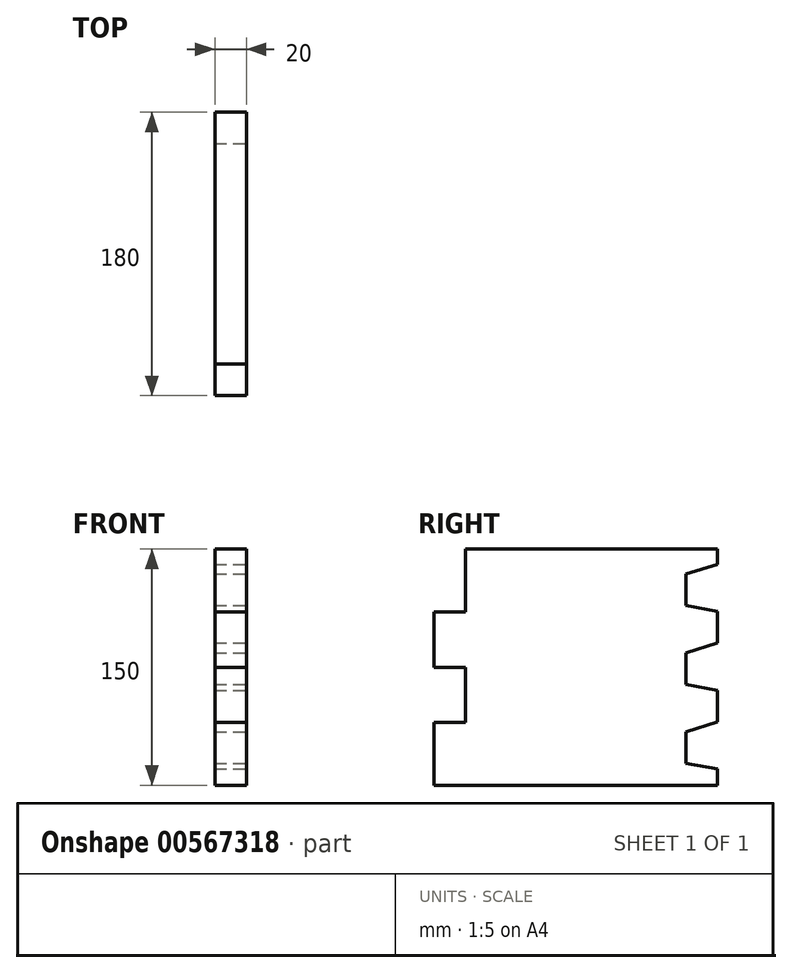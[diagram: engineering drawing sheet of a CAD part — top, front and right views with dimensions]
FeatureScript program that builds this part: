
annotation { "Feature Type Name" : "Feature", "Feature Type Description" : "" }
export const myFeature = defineFeature(function(context is Context, id is Id, definition is map)
    precondition{}
    {
        {
            var Q0;
            Q0=qCreatedBy(makeId("Front.planeOp"),FACE);
            var sketch = newSketch(context, id + "F0", { "sketchPlane" : qUnion([Q0])});
            skLineSegment(sketch, "E0.bottom", {"start": v(0, 0) * mm, "end": v(-180, 0) * mm});
            skLineSegment(sketch, "E0.top", {"start": v(0, 150) * mm, "end": v(-160, 150) * mm});
            skLineSegment(sketch, "E0.left", {"start": v(0, 0) * mm, "end": v(0, 150) * mm});
            skLineSegment(sketch, "E0.right", {"start": v(-180, 0) * mm, "end": v(-180, 40) * mm});
            skLineSegment(sketch, "E1", {"start": v(-160, 150) * mm, "end": v(-160, 0) * mm});
            skLineSegment(sketch, "E2", {"start": v(-180, 75) * mm, "end": v(-160, 75) * mm});
            skLineSegment(sketch, "E3", {"start": v(-160, 110) * mm, "end": v(-180, 110) * mm});
            skLineSegment(sketch, "E4", {"start": v(-160, 40) * mm, "end": v(-180, 40) * mm});
            skPoint(sketch, "E5.orphan", {"position": v(-180, 150) * mm});
            skLineSegment(sketch, "E6.trimOffspring", {"start": v(-180, 75) * mm, "end": v(-180, 110) * mm});
            skSolve(sketch);
        }
        {
            var Q0;
            Q0 = qSketchRegion(id + "F0", true);
            extrude(context, id + "F1", {"entities" : qUnion([Q0]), "depth" : 20 * mm, "offsetDistance" : 25 * mm});
        }
        {
            var Q0;
            Q0=makeQuery(id+"F1.opExtrude","SWEPT_FACE",FACE,{"disambiguationData":[OSD([sQuery(id+"F0.wireOp",EDGE,"E0.left")])]});
            var sketch = newSketch(context, id + "F2", { "sketchPlane" : qUnion([Q0])});
            skLineSegment(sketch, "E7", {"start": v(-20, 75) * mm, "end": v(0, 75) * mm});
            skLineSegment(sketch, "E8", {"start": v(-20, 60) * mm, "end": v(0, 65) * mm});
            skLineSegment(sketch, "E9", {"start": v(0, 85) * mm, "end": v(-20, 90) * mm});
            skLineSegment(sketch, "E10", {"start": v(-20, 90) * mm, "end": v(-20, 110) * mm});
            skLineSegment(sketch, "E11", {"start": v(0, 85) * mm, "end": v(0, 115) * mm});
            skLineSegment(sketch, "E12", {"start": v(0, 115) * mm, "end": v(-20, 110) * mm});
            skLineSegment(sketch, "E13", {"start": v(-20, 110) * mm, "end": v(-20, 140) * mm});
            skLineSegment(sketch, "E14", {"start": v(-20, 140) * mm, "end": v(0, 135) * mm});
            skLineSegment(sketch, "E15", {"start": v(0, 135) * mm, "end": v(0, 115) * mm});
            skLineSegment(sketch, "E16", {"start": v(-20, 60) * mm, "end": v(-20, 40) * mm});
            skLineSegment(sketch, "E17", {"start": v(-20, 40) * mm, "end": v(0, 35) * mm});
            skLineSegment(sketch, "E18", {"start": v(0, 35) * mm, "end": v(0, 65) * mm});
            skLineSegment(sketch, "E19", {"start": v(0, 35) * mm, "end": v(0, 15) * mm});
            skLineSegment(sketch, "E20", {"start": v(0, 15) * mm, "end": v(-20, 10) * mm});
            skLineSegment(sketch, "E21", {"start": v(-20, 10) * mm, "end": v(-20, 40) * mm});
            skSolve(sketch);
        }
        {
            var Q0;
            Q0=makeQuery(id+"F1.opExtrude","SWEPT_BODY",BODY,{"disambiguationData":[OSD([sQuery(id+"F0.wireOp",EDGE,"E0.bottom"),sQuery(id+"F0.wireOp",EDGE,"E0.top"),sQuery(id+"F0.wireOp",EDGE,"E0.left"),sQuery(id+"F0.wireOp",EDGE,"E0.right"),sQuery(id+"F0.wireOp",EDGE,"E1"),sQuery(id+"F0.wireOp",EDGE,"E2"),sQuery(id+"F0.wireOp",EDGE,"E3"),sQuery(id+"F0.wireOp",EDGE,"E4"),sQuery(id+"F0.wireOp",EDGE,"E6.trimOffspring")])]});
            var Q1;
            {var subQ0=sQuery(id+"F0.wireOp",EDGE,"E0.left");Q1=makeQuery(id+"F11KBl5U0m4TjAi_1.boolean.opBoolean","SPLIT",EDGE,{"disambiguationData":[TD([makeQuery(id+"F11KBl5U0m4TjAi_1.opExtrude","SWEPT_FACE",FACE,{"disambiguationData":[OSD([sQuery(id+"F2.wireOp",EDGE,"E9")])]})])],"derivedFrom":makeQuery(id+"F1.opExtrude","CAP_EDGE",EDGE,{"disambiguationData":[OSD([subQ0])],"isStart":false})});}
            transform(context, id + "F3", {"entities" : qUnion([Q0]), "transformType" : TransformType.ROTATION, "transformAxis" : qUnion([Q1]), "angle" : 90 * degree, "makeCopy" : false});
        }
        {
            var Q0;
            Q0=makeQuery(id+"F1.opExtrude","CAP_FACE",FACE,{"disambiguationData":[OSD([sQuery(id+"F0.wireOp",EDGE,"E0.bottom"),sQuery(id+"F0.wireOp",EDGE,"E0.top"),sQuery(id+"F0.wireOp",EDGE,"E0.left"),sQuery(id+"F0.wireOp",EDGE,"E0.right"),sQuery(id+"F0.wireOp",EDGE,"E1"),sQuery(id+"F0.wireOp",EDGE,"E2"),sQuery(id+"F0.wireOp",EDGE,"E3"),sQuery(id+"F0.wireOp",EDGE,"E4"),sQuery(id+"F0.wireOp",EDGE,"E6.trimOffspring")])],"isStart":false});
            var sketch = newSketch(context, id + "F4", { "sketchPlane" : qUnion([Q0])});
            skLineSegment(sketch, "E22.MirrorCS", {"start": v(-20, 40.4) * mm, "end": v(-20, 10.4) * mm});
            skLineSegment(sketch, "E23.MirrorCS", {"start": v(-40, 114.26) * mm, "end": v(-20, 110.4) * mm});
            skLineSegment(sketch, "E24.MirrorCS", {"start": v(-20, 110.4) * mm, "end": v(-20, 90.4) * mm});
            skLineSegment(sketch, "E25.MirrorCS", {"start": v(-20, 90.4) * mm, "end": v(-40, 84.04) * mm});
            skLineSegment(sketch, "E26.MirrorCS", {"start": v(-20, 90.4) * mm, "end": v(-20, 60.4) * mm});
            skLineSegment(sketch, "E27.MirrorCS", {"start": v(-20, 60.4) * mm, "end": v(-40, 64.04) * mm});
            skLineSegment(sketch, "E28.MirrorCS", {"start": v(-20, 110.4) * mm, "end": v(-20, 140.4) * mm});
            skLineSegment(sketch, "E29.MirrorCS", {"start": v(-20, 140.4) * mm, "end": v(-40, 134.26) * mm});
            skLineSegment(sketch, "E30.MirrorCS", {"start": v(-20, 60.4) * mm, "end": v(-20, 40.4) * mm});
            skLineSegment(sketch, "E31.MirrorCS", {"start": v(-20, 40.4) * mm, "end": v(-40, 34.04) * mm});
            skLineSegment(sketch, "E32.MirrorCS", {"start": v(-20, 10.4) * mm, "end": v(-40, 14.04) * mm});
            skLineSegment(sketch, "E33", {"start": v(-40, 134.26) * mm, "end": v(-40, 114.26) * mm});
            skLineSegment(sketch, "E34", {"start": v(-40, 84.04) * mm, "end": v(-40, 64.04) * mm});
            skLineSegment(sketch, "E35", {"start": v(-40, 34.04) * mm, "end": v(-40, 14.04) * mm});
            skSolve(sketch);
        }
        {
            var Q0;
            Q0=makeQuery(id+"F4.imprint","IMPRINT",FACE,{"disambiguationData":[TD([[makeQuery(id+"F4.imprint","IMPRINT",EDGE,{"derivedFrom":sQuery(id+"F4.wireOp",EDGE,"E23.MirrorCS")}),1.0]])]});
            var Q1;
            Q1=makeQuery(id+"F4.imprint","IMPRINT",FACE,{"disambiguationData":[TD([[makeQuery(id+"F4.imprint","IMPRINT",EDGE,{"derivedFrom":sQuery(id+"F4.wireOp",EDGE,"E25.MirrorCS")}),1.0]])]});
            var Q2;
            Q2=makeQuery(id+"F4.imprint","IMPRINT",FACE,{"disambiguationData":[TD([[makeQuery(id+"F4.imprint","IMPRINT",EDGE,{"derivedFrom":sQuery(id+"F4.wireOp",EDGE,"E22.MirrorCS")}),1.0]])]});
            extrude(context, id + "F5", {"entities" : qUnion([Q0, Q1, Q2]), "operationType" : NewBodyOperationType.REMOVE, "endBound" : BoundingType.THROUGH_ALL, "oppositeDirection" : true, "depth" : 20 * mm, "offsetDistance" : 25 * mm});
        }
    });
